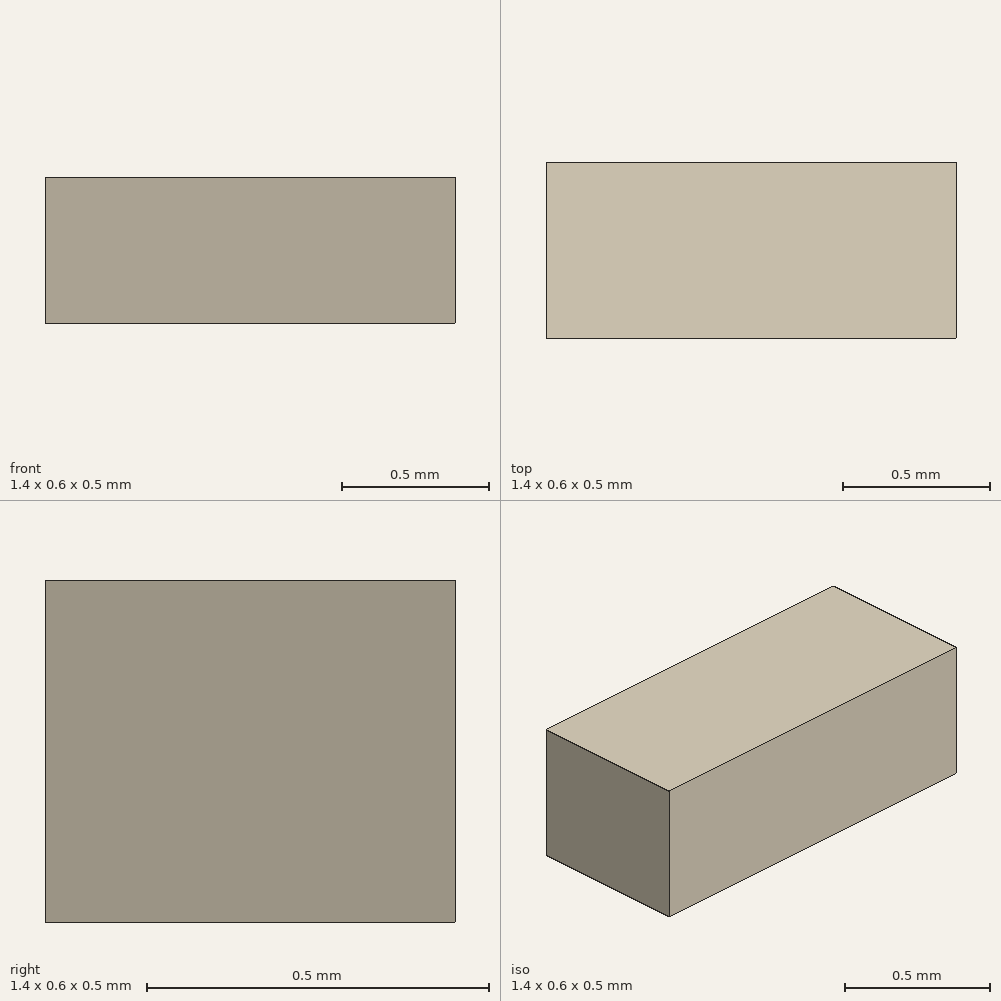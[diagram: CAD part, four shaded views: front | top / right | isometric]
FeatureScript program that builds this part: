
annotation { "Feature Type Name" : "Feature", "Feature Type Description" : "" }
export const myFeature = defineFeature(function(context is Context, id is Id, definition is map)
    precondition{}
    {
        {
            var Q0;
            Q0=qCreatedBy(makeId("Top.planeOp"),FACE);
            var sketch = newSketch(context, id + "F0", { "sketchPlane" : qUnion([Q0])});
            skLineSegment(sketch, "E0.bottom", {"start": v(0, 0) * mm, "end": v(1.4, 0) * mm});
            skLineSegment(sketch, "E0.top", {"start": v(0, 0.6) * mm, "end": v(1.4, 0.6) * mm});
            skLineSegment(sketch, "E0.left", {"start": v(0, 0) * mm, "end": v(0, 0.6) * mm});
            skLineSegment(sketch, "E0.right", {"start": v(1.4, 0) * mm, "end": v(1.4, 0.6) * mm});
            skSolve(sketch);
        }
        {
            var Q0;
            Q0=makeQuery(id+"F0.imprint","IMPRINT",FACE,{"disambiguationData":[TD([[makeQuery(id+"F0.imprint","IMPRINT",EDGE,{"derivedFrom":sQuery(id+"F0.wireOp",EDGE,"E0.bottom")}),1.0]])]});
            extrude(context, id + "F1", {"entities" : qUnion([Q0]), "depth" : 0.5 * mm});
        }
    });
